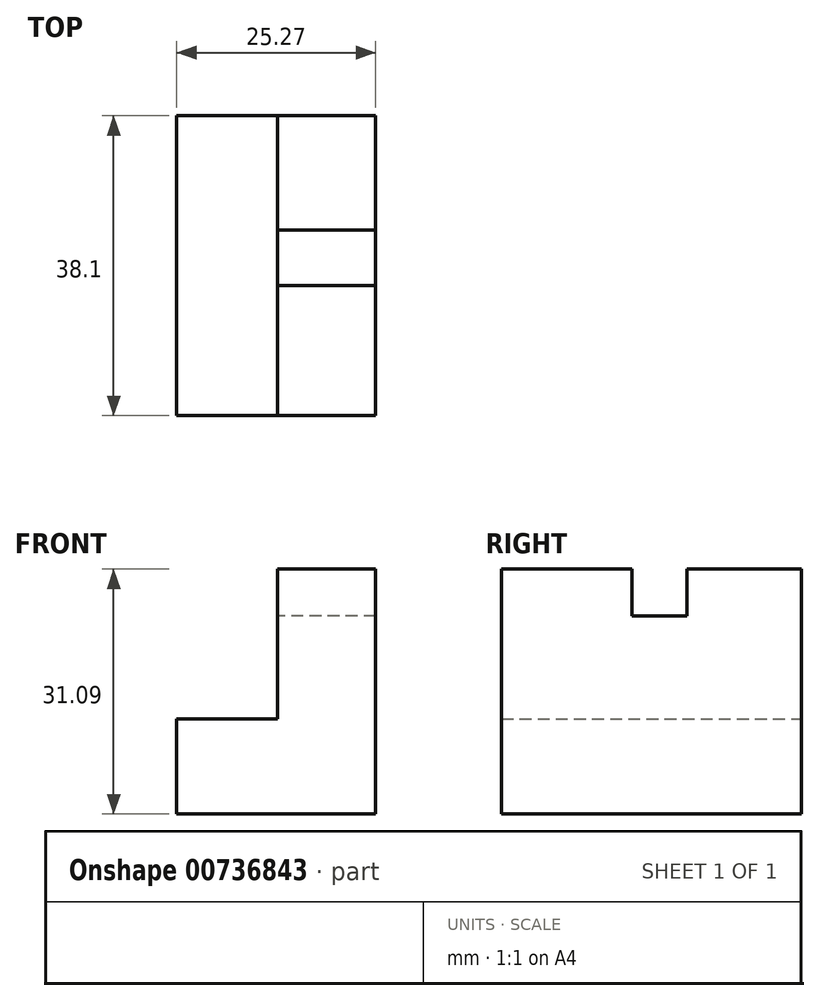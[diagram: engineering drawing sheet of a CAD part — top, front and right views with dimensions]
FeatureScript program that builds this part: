
annotation { "Feature Type Name" : "Feature", "Feature Type Description" : "" }
export const myFeature = defineFeature(function(context is Context, id is Id, definition is map)
    precondition{}
    {
        {
            var Q0;
            Q0=qCreatedBy(makeId("Front.planeOp"),FACE);
            var sketch = newSketch(context, id + "F0", { "sketchPlane" : qUnion([Q0])});
            skLineSegment(sketch, "E0", {"start": v(0, 0) * mm, "end": v(25.27, 0) * mm});
            skLineSegment(sketch, "E1", {"start": v(25.27, 0) * mm, "end": v(25.27, 31.75) * mm});
            skLineSegment(sketch, "E2", {"start": v(25.53, 31.09) * mm, "end": v(12.83, 31.09) * mm});
            skLineSegment(sketch, "E3", {"start": v(12.83, 31.09) * mm, "end": v(12.83, 12.04) * mm});
            skLineSegment(sketch, "E4", {"start": v(12.83, 12.04) * mm, "end": v(0, 12.04) * mm});
            skLineSegment(sketch, "E5", {"start": v(0, 12.04) * mm, "end": v(0, 0) * mm});
            skSolve(sketch);
        }
        {
            var Q0;
            {var subQ4=sQuery(id+"F0.wireOp",EDGE,"E0");Q0=makeQuery(id+"F0.imprint","IMPRINT",FACE,{"disambiguationData":[TD([[makeQuery(id+"F0.imprint","IMPRINT",EDGE,{"derivedFrom":subQ4}),1.0]])]});}
            extrude(context, id + "F1", {"entities" : qUnion([Q0]), "depth" : 38.1 * mm, "offsetDistance" : 25.4 * mm});
        }
        {
            var Q0;
            Q0=qCreatedBy(makeId("Right.planeOp"),FACE);
            var sketch = newSketch(context, id + "F2", { "sketchPlane" : qUnion([Q0])});
            skLineSegment(sketch, "E6", {"start": v(-12.25, 30.86) * mm, "end": v(-12.25, 22.17) * mm});
            skLineSegment(sketch, "E7", {"start": v(-12.25, 22.17) * mm, "end": v(-24.65, 22.17) * mm});
            skLineSegment(sketch, "E8", {"start": v(-24.65, 22.17) * mm, "end": v(-24.65, 31.17) * mm});
            skLineSegment(sketch, "E9", {"start": v(-24.65, 31.17) * mm, "end": v(-12.25, 30.86) * mm});
            skSolve(sketch);
        }
        {
            var Q0;
            Q0=makeQuery(id+"F2.imprint","IMPRINT",FACE,{"disambiguationData":[TD([[makeQuery(id+"F2.imprint","IMPRINT",EDGE,{"derivedFrom":sQuery(id+"F2.wireOp",EDGE,"E6")}),-1.0]])]});
            extrude(context, id + "F3", {"entities" : qUnion([Q0]), "operationType" : NewBodyOperationType.REMOVE, "oppositeDirection" : true, "depth" : 12.7 * mm, "offsetDistance" : 25.4 * mm});
        }
        {
            var Q0;
            Q0=makeQuery(id+"F1.opExtrude","SWEPT_FACE",FACE,{"disambiguationData":[OSD([sQuery(id+"F0.wireOp",EDGE,"E3")])]});
            var sketch = newSketch(context, id + "F4", { "sketchPlane" : qUnion([Q0])});
            skLineSegment(sketch, "E10", {"start": v(14.54, 31.09) * mm, "end": v(14.54, 25.11) * mm});
            skLineSegment(sketch, "E11", {"start": v(14.54, 25.11) * mm, "end": v(21.55, 25.11) * mm});
            skLineSegment(sketch, "E12", {"start": v(21.55, 25.11) * mm, "end": v(21.55, 31.09) * mm});
            skLineSegment(sketch, "E13", {"start": v(21.55, 31.09) * mm, "end": v(14.54, 31.09) * mm});
            skSolve(sketch);
        }
        {
            var Q0;
            Q0=makeQuery(id+"F4.imprint","IMPRINT",FACE,{"disambiguationData":[TD([[makeQuery(id+"F4.imprint","IMPRINT",EDGE,{"derivedFrom":sQuery(id+"F4.wireOp",EDGE,"E10")}),1.0]])]});
            extrude(context, id + "F5", {"entities" : qUnion([Q0]), "operationType" : NewBodyOperationType.REMOVE, "oppositeDirection" : true, "depth" : 12.7 * mm, "offsetDistance" : 25.4 * mm});
        }
    });
